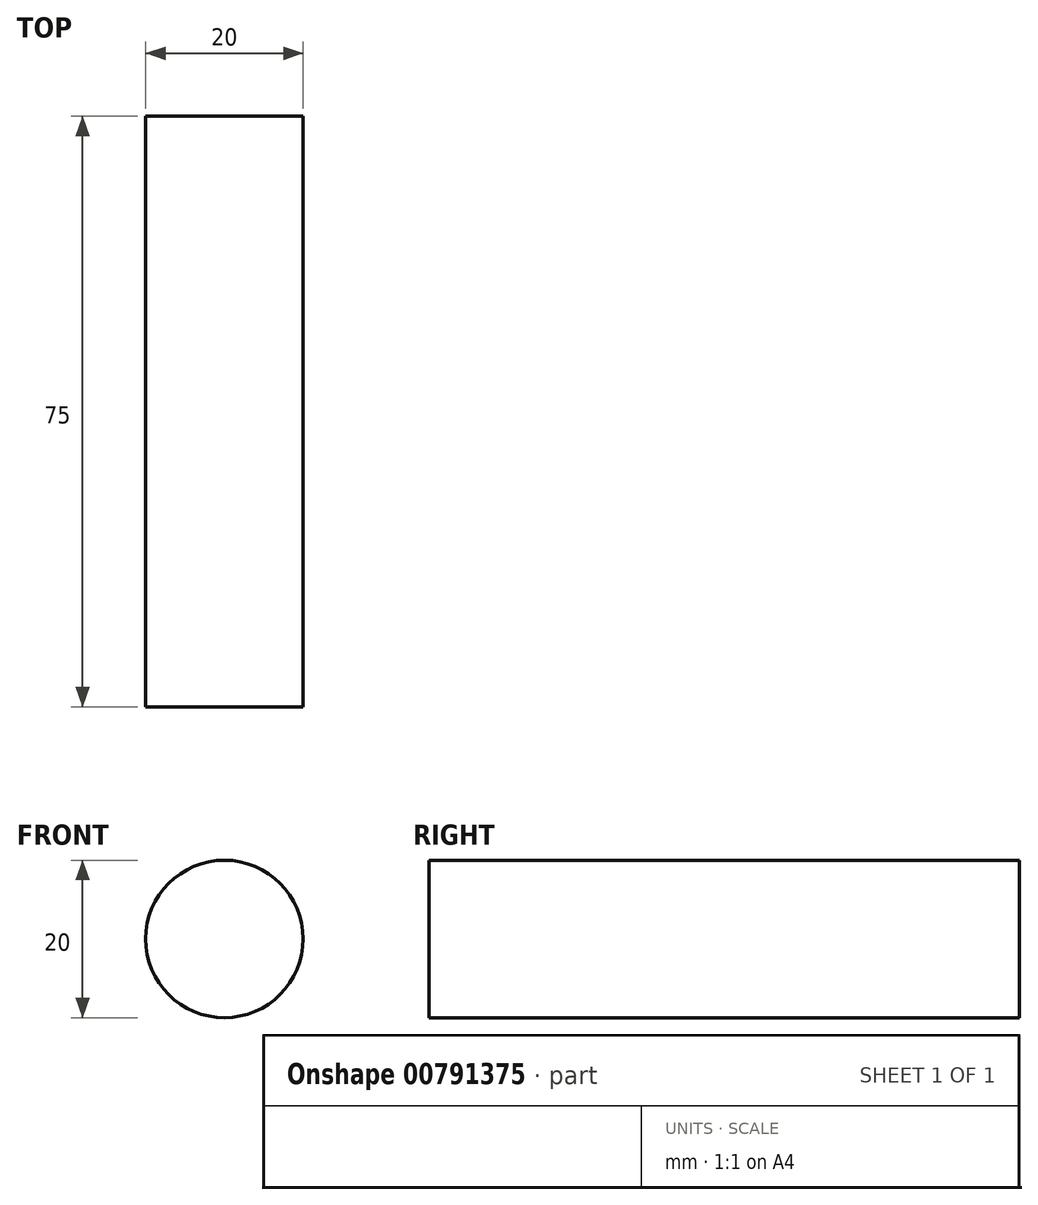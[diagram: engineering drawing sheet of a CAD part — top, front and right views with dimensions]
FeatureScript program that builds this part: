
annotation { "Feature Type Name" : "Feature", "Feature Type Description" : "" }
export const myFeature = defineFeature(function(context is Context, id is Id, definition is map)
    precondition{}
    {
        {
            var Q0;
            Q0=qCreatedBy(makeId("Front.planeOp"),FACE);
            var sketch = newSketch(context, id + "F0", { "sketchPlane" : qUnion([Q0])});
            skCircle(sketch, "E0", {"center": v(0, 0) * mm, "radius": 10 * mm});
            skSolve(sketch);
        }
        {
            var Q0;
            Q0 = qSketchRegion(id + "F0", true);
            extrude(context, id + "F1", {"entities" : qUnion([Q0]), "depth" : 75 * mm, "offsetDistance" : 25 * mm});
        }
    });
